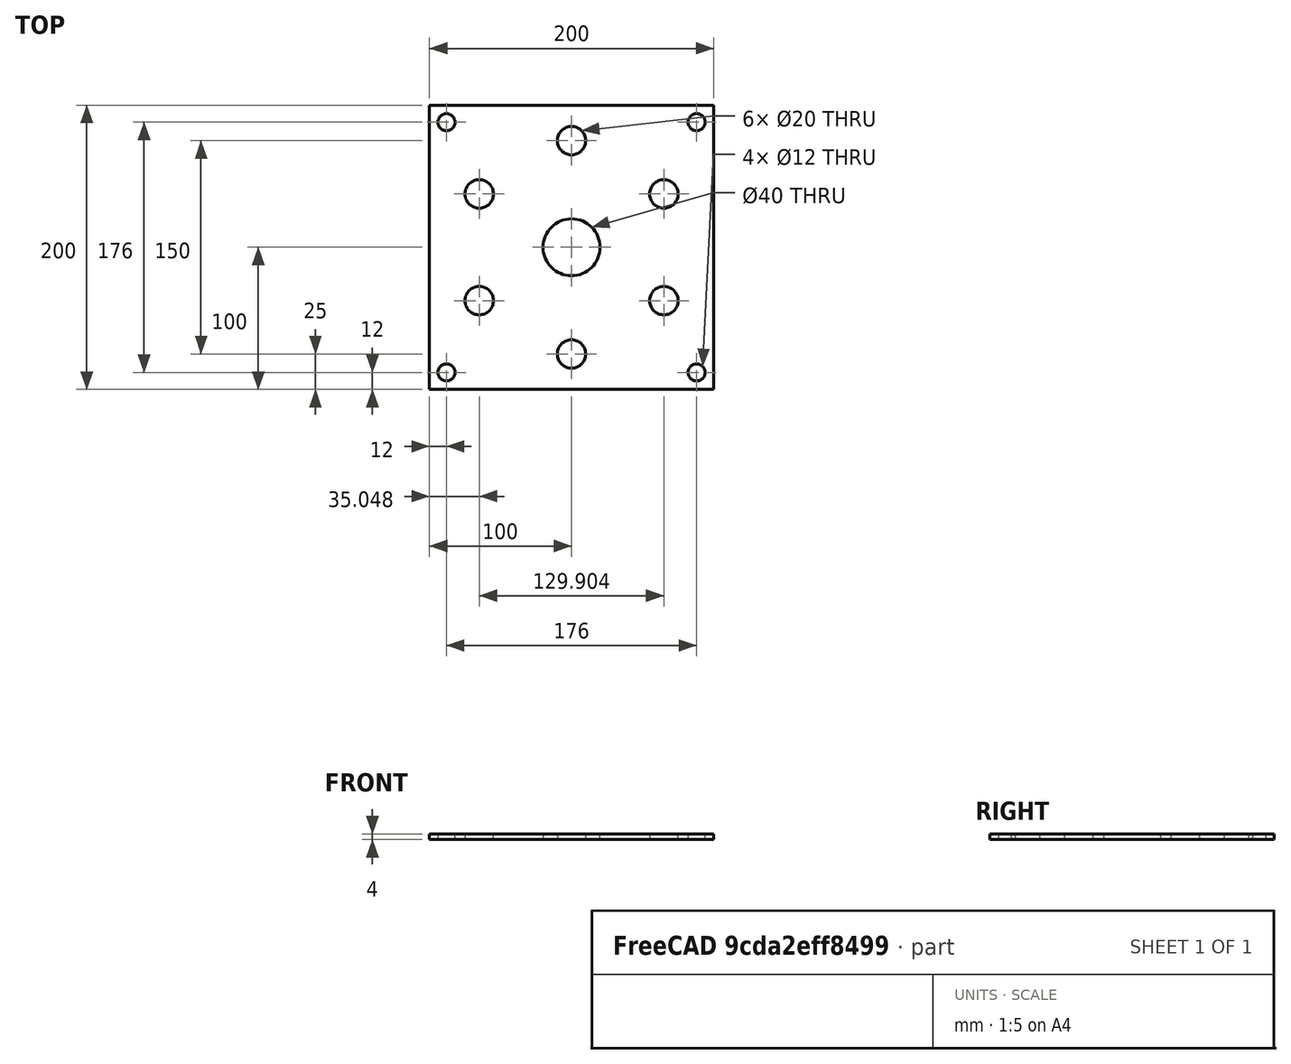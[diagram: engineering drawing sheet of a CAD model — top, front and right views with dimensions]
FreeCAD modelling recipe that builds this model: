
FCSTD DOCUMENT  (FreeCAD 0.17R12794 (Git))
Label: robot17
License: All rights reserved
LicenseURL: http://en.wikipedia.org/wiki/All_rights_reserved
objects: PartDesign::Body×2, Sketcher::SketchObject×1, PartDesign::Pad×1, PartDesign::Plane×1, PartDesign::ShapeBinder×1, PartDesign::Point×1
note: 8 computed .brp shape members not serialized (recipe doc carries the construction recipe); baked Part::Feature solids carry a one-line shape summary decoded from their .brp

FEATURE [Sketcher::SketchObject] Sketch001
  MapMode = 5
  sketch-geometry (22):
    g0: LineSegment StartX=0 StartY=0 StartZ=0 EndX=200 EndY=0 EndZ=0
    g1: LineSegment StartX=200 StartY=0 StartZ=0 EndX=200 EndY=200 EndZ=0
    g2: LineSegment StartX=200 StartY=200 StartZ=0 EndX=0 EndY=200 EndZ=0
    g3: LineSegment StartX=0 StartY=200 StartZ=0 EndX=0 EndY=0 EndZ=0
    g4: Circle CenterX=12 CenterY=12 CenterZ=0 NormalX=0 NormalY=0 NormalZ=1 AngleXU=0 Radius=6
    g5: Circle CenterX=12 CenterY=188 CenterZ=0 NormalX=0 NormalY=0 NormalZ=1 AngleXU=0 Radius=6
    g6: Circle CenterX=188 CenterY=188 CenterZ=0 NormalX=0 NormalY=0 NormalZ=1 AngleXU=0 Radius=6
    g7: Circle CenterX=188 CenterY=12 CenterZ=0 NormalX=0 NormalY=0 NormalZ=1 AngleXU=0 Radius=6
    g8: LineSegment [constr] StartX=164.952 StartY=62.5 StartZ=0 EndX=164.952 EndY=137.5 EndZ=0
    g9: LineSegment [constr] StartX=164.952 StartY=137.5 StartZ=0 EndX=100 EndY=175 EndZ=0
    g10: LineSegment [constr] StartX=100 StartY=175 StartZ=0 EndX=35.0481 EndY=137.5 EndZ=0
    g11: LineSegment [constr] StartX=35.0481 StartY=137.5 StartZ=0 EndX=35.0481 EndY=62.5 EndZ=0
    g12: LineSegment [constr] StartX=35.0481 StartY=62.5 StartZ=0 EndX=100 EndY=25 EndZ=0
    g13: LineSegment [constr] StartX=100 StartY=25 StartZ=0 EndX=164.952 EndY=62.5 EndZ=0
    g14: Circle [constr] CenterX=100 CenterY=100 CenterZ=0 NormalX=0 NormalY=0 NormalZ=1 AngleXU=0 Radius=75
    g15: Circle CenterX=100 CenterY=175 CenterZ=0 NormalX=0 NormalY=0 NormalZ=1 AngleXU=0 Radius=10
    g16: Circle CenterX=35.0481 CenterY=137.5 CenterZ=0 NormalX=0 NormalY=0 NormalZ=1 AngleXU=0 Radius=10
    g17: Circle CenterX=35.0481 CenterY=62.5 CenterZ=0 NormalX=0 NormalY=0 NormalZ=1 AngleXU=0 Radius=10
    g18: Circle CenterX=100 CenterY=25 CenterZ=0 NormalX=0 NormalY=0 NormalZ=1 AngleXU=0 Radius=10
    g19: Circle CenterX=164.952 CenterY=62.5 CenterZ=0 NormalX=0 NormalY=0 NormalZ=1 AngleXU=0 Radius=10
    g20: Circle CenterX=164.952 CenterY=137.5 CenterZ=0 NormalX=0 NormalY=0 NormalZ=1 AngleXU=0 Radius=10
    g21: Circle CenterX=100 CenterY=100 CenterZ=0 NormalX=0 NormalY=0 NormalZ=1 AngleXU=0 Radius=20
  constraints (54):
    c: Coincident(g0,g1)
    c: Coincident(g1,g2)
    c: Coincident(g2,g3)
    c: Coincident(g3,g0)
    c: Horizontal(g0)
    c: Horizontal(g2)
    c: Vertical(g1)
    c: Vertical(g3)
    c: Coincident(g0,g-1)
    c: DistanceY(g1,g1) = 200
    c: DistanceX(g2,g2) = 200
    c: Radius(g4) = 6
    c: Equal(g4,g5) = 6
    c: DistanceY(g-1,g4) = 12
    c: DistanceX(g-1,g4) = 12
    c: Equal(g5,g6)
    c: Equal(g6,g7)
    c: DistanceY(g4,g7) = 0
    c: DistanceX(g4,g5) = 0
    c: DistanceY(g5,g6) = 0
    c: DistanceX(g6,g7) = 0
    c: DistanceX(g7,g0) = 12
    c: DistanceY(g6,g1) = 12
    c: Coincident(g8,g9)
    c: Coincident(g9,g10)
    c: Coincident(g10,g11)
    c: Coincident(g11,g12)
    c: Coincident(g12,g13)
    c: Coincident(g13,g8)
    c: Equal(g8, g9-g13) x5
    c: PointOnObject(g8,g14)
    c: PointOnObject(g9,g14)
    c: PointOnObject(g10,g14)
    c: PointOnObject(g11,g14)
    c: PointOnObject(g12,g14)
    c: PointOnObject(g13,g14)
    c: DistanceX(g-1,g14) = 100
    c: DistanceY(g-1,g14) = 100
    c: Parallel(g11,g3)
    c: Radius(g14) = 75
    c: Radius(g15) = 10
    c: Coincident(g15,g9)
    c: Equal(g15,g16)
    c: Equal(g16,g17)
    c: Equal(g17,g18)
    c: Equal(g18,g19)
    c: Equal(g19,g20)
    c: Coincident(g16,g10)
    c: Coincident(g17,g11)
    c: Coincident(g18,g12)
    c: Coincident(g19,g8)
    c: Coincident(g20,g8)
    c: Coincident(g21,g14)
    c: Radius(g21) = 20
FEATURE [PartDesign::Pad] Pad
  Length = 4
  Length2 = 100
  Profile = -> Sketch001
  Type = 0
FEATURE [PartDesign::Plane] DatumPlane
  MapMode = 5
  Placement = pos=(0,0,4) rot=(0,0,1;0rad)
  Support = -> [Pad]
FEATURE [PartDesign::Body] Body  label="Bottom"
  Group = -> [Sketch001,Pad,DatumPlane]
  Origin = -> Origin
  Tip = -> Pad
FEATURE [PartDesign::ShapeBinder] CopyPad
  Placement = pos=(0,0,4) rot=(0,0,1;0rad)
FEATURE [PartDesign::Point] DatumPoint
  AttacherType = Attacher::AttachEnginePoint
  MapMode = 36
  Placement = pos=(100,100,4) rot=(1,0,0;1.5708rad)
  Support = -> [CopyPad]
FEATURE [PartDesign::Body] Body001
  Group = -> [DatumPoint]
  Origin = -> Origin001
